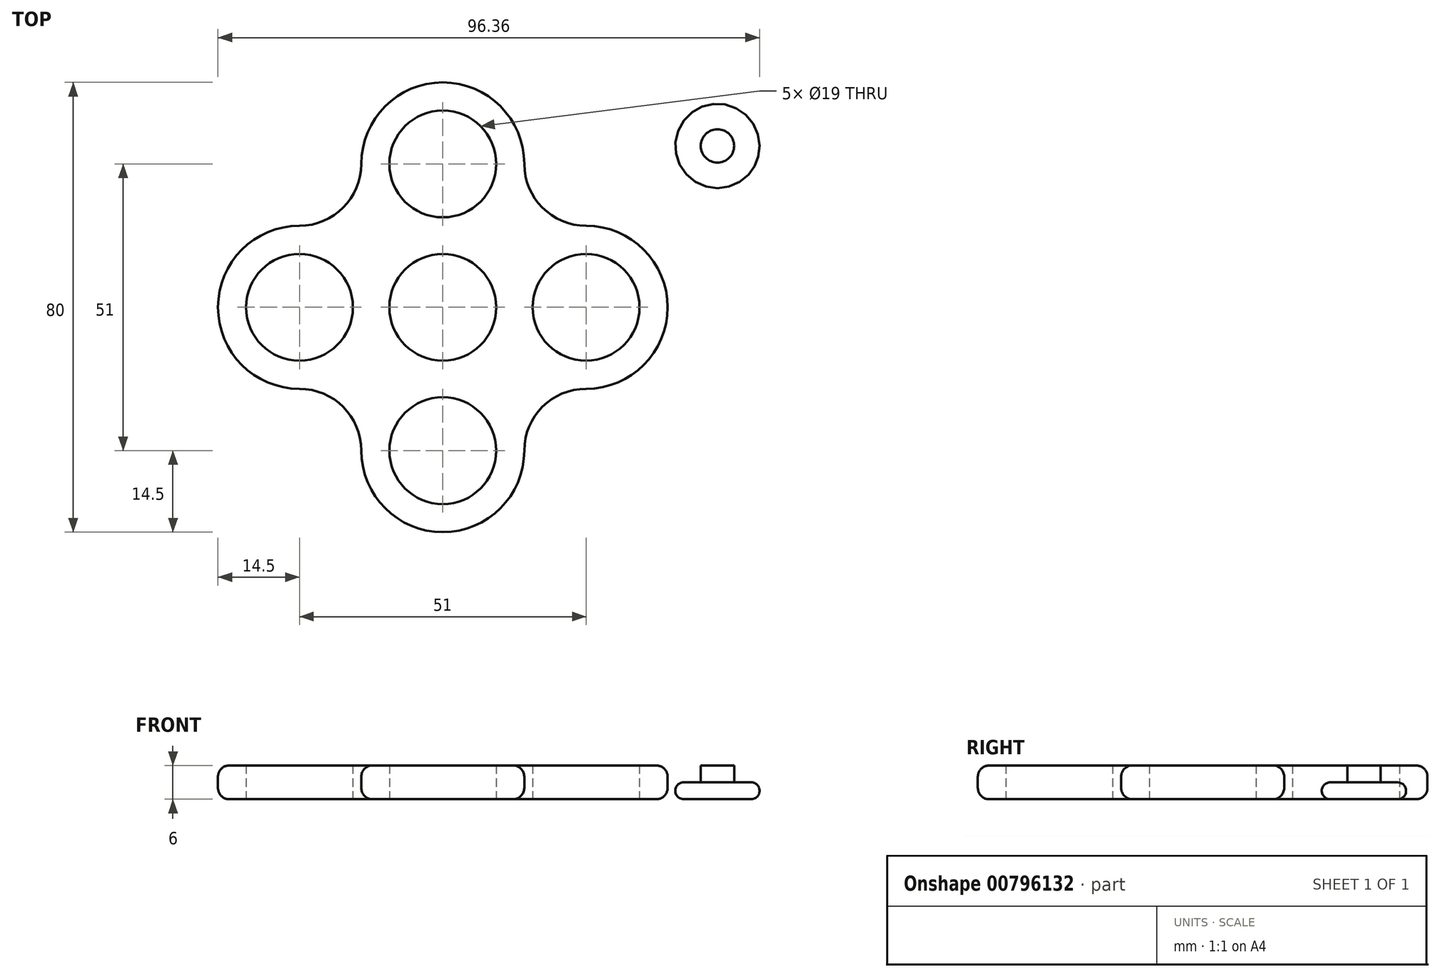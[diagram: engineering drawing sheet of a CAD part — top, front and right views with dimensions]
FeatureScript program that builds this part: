
annotation { "Feature Type Name" : "Feature", "Feature Type Description" : "" }
export const myFeature = defineFeature(function(context is Context, id is Id, definition is map)
    precondition{}
    {
        {
            var Q0;
            Q0=qCreatedBy(makeId("Top.planeOp"),FACE);
            var sketch = newSketch(context, id + "F0", { "sketchPlane" : qUnion([Q0])});
            skLineSegment(sketch, "E0", {"start": v(0, 25.5) * mm, "end": v(0, -25.5) * mm, "construction": true});
            skLineSegment(sketch, "E1", {"start": v(-25.5, 0) * mm, "end": v(25.5, 0) * mm, "construction": true});
            skCircle(sketch, "E2", {"center": v(-25.5, 0) * mm, "radius": 9.5 * mm});
            skCircle(sketch, "E3", {"center": v(0, -25.5) * mm, "radius": 9.5 * mm});
            skCircle(sketch, "E4", {"center": v(25.5, 0) * mm, "radius": 9.5 * mm});
            skCircle(sketch, "E5", {"center": v(0, 25.5) * mm, "radius": 9.5 * mm});
            skCircle(sketch, "E6", {"center": v(0, 0) * mm, "radius": 9.5 * mm});
            skArc(sketch, "E7.0", {"start": v(14.5, 25.5) * mm, "mid": v(0, 40) * mm, "end": v(-14.5, 25.5) * mm});
            skArc(sketch, "E8.0", {"start": v(-25.5, 14.5) * mm, "mid": v(-17.72, 17.72) * mm, "end": v(-14.5, 25.5) * mm});
            skArc(sketch, "E9.0", {"start": v(-25.5, 14.5) * mm, "mid": v(-40, 0) * mm, "end": v(-25.5, -14.5) * mm});
            skArc(sketch, "E10.0", {"start": v(-14.5, -25.5) * mm, "mid": v(-17.72, -17.72) * mm, "end": v(-25.5, -14.5) * mm});
            skArc(sketch, "E11.0", {"start": v(-14.5, -25.5) * mm, "mid": v(0, -40) * mm, "end": v(14.5, -25.5) * mm});
            skArc(sketch, "E12.0", {"start": v(14.5, -25.5) * mm, "mid": v(17.72, -17.72) * mm, "end": v(25.5, -14.5) * mm});
            skArc(sketch, "E13.0", {"start": v(25.5, -14.5) * mm, "mid": v(40, 0) * mm, "end": v(25.5, 14.5) * mm});
            skArc(sketch, "E14.0", {"start": v(14.5, 25.5) * mm, "mid": v(17.72, 17.72) * mm, "end": v(25.5, 14.5) * mm});
            skPoint(sketch, "E15.end.orphan", {"position": v(25.5, 9.5) * mm});
            skPoint(sketch, "E16.orphan", {"position": v(-9.5, 25.5) * mm});
            skSolve(sketch);
        }
        {
            var Q0;
            Q0=makeQuery(id+"F0.imprint","IMPRINT",FACE,{"disambiguationData":[TD([[makeQuery(id+"F0.imprint","IMPRINT",EDGE,{"derivedFrom":sQuery(id+"F0.wireOp",EDGE,"E2")}),-1.0]])]});
            extrude(context, id + "F1", {"entities" : qUnion([Q0]), "depth" : 6 * mm, "offsetDistance" : 25.4 * mm});
        }
        {
            var Q0;
            Q0=makeQuery(id+"F1.opExtrude","CAP_EDGE",EDGE,{"disambiguationData":[OSD([sQuery(id+"F0.wireOp",EDGE,"E9.0")])],"isStart":false});
            var Q1;
            Q1=makeQuery(id+"F1.opExtrude","CAP_EDGE",EDGE,{"disambiguationData":[OSD([sQuery(id+"F0.wireOp",EDGE,"E10.0")])],"isStart":false});
            var Q2;
            Q2=makeQuery(id+"F1.opExtrude","CAP_EDGE",EDGE,{"disambiguationData":[OSD([sQuery(id+"F0.wireOp",EDGE,"E11.0")])],"isStart":false});
            var Q3;
            Q3=makeQuery(id+"F1.opExtrude","CAP_EDGE",EDGE,{"disambiguationData":[OSD([sQuery(id+"F0.wireOp",EDGE,"E12.0")])],"isStart":false});
            var Q4;
            Q4=makeQuery(id+"F1.opExtrude","CAP_EDGE",EDGE,{"disambiguationData":[OSD([sQuery(id+"F0.wireOp",EDGE,"E13.0")])],"isStart":false});
            var Q5;
            Q5=makeQuery(id+"F1.opExtrude","CAP_EDGE",EDGE,{"disambiguationData":[OSD([sQuery(id+"F0.wireOp",EDGE,"E14.0")])],"isStart":false});
            var Q6;
            Q6=makeQuery(id+"F1.opExtrude","CAP_EDGE",EDGE,{"disambiguationData":[OSD([sQuery(id+"F0.wireOp",EDGE,"E11.0")])],"isStart":true});
            var Q7;
            Q7=makeQuery(id+"F1.opExtrude","CAP_EDGE",EDGE,{"disambiguationData":[OSD([sQuery(id+"F0.wireOp",EDGE,"E10.0")])],"isStart":true});
            var Q8;
            Q8=makeQuery(id+"F1.opExtrude","CAP_EDGE",EDGE,{"disambiguationData":[OSD([sQuery(id+"F0.wireOp",EDGE,"E9.0")])],"isStart":true});
            var Q9;
            Q9=makeQuery(id+"F1.opExtrude","CAP_EDGE",EDGE,{"disambiguationData":[OSD([sQuery(id+"F0.wireOp",EDGE,"E12.0")])],"isStart":true});
            var Q10;
            Q10=makeQuery(id+"F1.opExtrude","CAP_EDGE",EDGE,{"disambiguationData":[OSD([sQuery(id+"F0.wireOp",EDGE,"E13.0")])],"isStart":true});
            var Q11;
            Q11=makeQuery(id+"F1.opExtrude","CAP_EDGE",EDGE,{"disambiguationData":[OSD([sQuery(id+"F0.wireOp",EDGE,"E14.0")])],"isStart":true});
            var Q12;
            Q12=makeQuery(id+"F1.opExtrude","CAP_EDGE",EDGE,{"disambiguationData":[OSD([sQuery(id+"F0.wireOp",EDGE,"E7.0")])],"isStart":true});
            var Q13;
            Q13=makeQuery(id+"F1.opExtrude","CAP_EDGE",EDGE,{"disambiguationData":[OSD([sQuery(id+"F0.wireOp",EDGE,"E7.0")])],"isStart":false});
            var Q14;
            Q14=makeQuery(id+"F1.opExtrude","CAP_EDGE",EDGE,{"disambiguationData":[OSD([sQuery(id+"F0.wireOp",EDGE,"E8.0")])],"isStart":false});
            var Q15;
            Q15=makeQuery(id+"F1.opExtrude","CAP_EDGE",EDGE,{"disambiguationData":[OSD([sQuery(id+"F0.wireOp",EDGE,"E8.0")])],"isStart":true});
            fillet(context, id + "F2", {"entities" : qUnion([Q0, Q1, Q2, Q3, Q4, Q5, Q6, Q7, Q8, Q9, Q10, Q11, Q12, Q13, Q14, Q15]), "radius" : 2 * mm, "tangentPropagation" : true, "allowEdgeOverflow" : false});
        }
        {
            var Q0;
            Q0=qCreatedBy(makeId("Top.planeOp"),FACE);
            var sketch = newSketch(context, id + "F3", { "sketchPlane" : qUnion([Q0])});
            skCircle(sketch, "E17", {"center": v(48.86, 28.7) * mm, "radius": 7.5 * mm});
            skCircle(sketch, "E18", {"center": v(48.86, 28.7) * mm, "radius": 2.96 * mm});
            skSolve(sketch);
        }
        {
            var Q0;
            Q0=makeQuery(id+"F3.imprint","IMPRINT",FACE,{"disambiguationData":[TD([[makeQuery(id+"F3.imprint","IMPRINT",EDGE,{"derivedFrom":sQuery(id+"F3.wireOp",EDGE,"E18")}),1.0]])]});
            extrude(context, id + "F4", {"entities" : qUnion([Q0]), "depth" : 6 * mm, "offsetDistance" : 25.4 * mm});
        }
        {
            var Q0;
            Q0 = qSketchRegion(id + "F3", true);
            extrude(context, id + "F5", {"entities" : qUnion([Q0]), "operationType" : NewBodyOperationType.ADD, "depth" : 3 * mm, "offsetDistance" : 25.4 * mm});
        }
        {
            var Q0;
            Q0=makeQuery(id+"F5.opExtrude","CAP_EDGE",EDGE,{"disambiguationData":[OSD([sQuery(id+"F3.wireOp",EDGE,"E17")])],"isStart":false});
            var Q1;
            Q1=makeQuery(id+"F5.opExtrude","CAP_EDGE",EDGE,{"disambiguationData":[OSD([sQuery(id+"F3.wireOp",EDGE,"E17")])],"isStart":true});
            fillet(context, id + "F6", {"entities" : qUnion([Q0, Q1]), "radius" : 1.5 * mm, "tangentPropagation" : true, "allowEdgeOverflow" : false});
        }
    });
